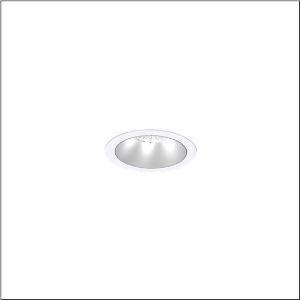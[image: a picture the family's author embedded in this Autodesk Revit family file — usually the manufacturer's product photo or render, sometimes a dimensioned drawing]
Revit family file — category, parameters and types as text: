
# Revit family: lunis_21_m_51db19tc91c
name_source: partatom
category: Lighting Fixtures
units: mm (PartAtom-declared; Revit-internal decimal feet)

## family parameters
Cut with Voids When Loaded = No
Host = Face
Light Source = No
Part Type = Normal
Room Calculation Point = No
Round Connector Dimension = Use Diameter
Shared = No

## types (1)
- --- (1 x LED, 3750 lm, 26 W, 4000K)
    Apparent Load = 26 VA
    CIE Flux Codes = 95 100 100 100 100
    Color Rendering = 80
    Color Temperature = 4000K
    Default Elevation = 1800 mm
    Description = Lunis 21,  M, downlight, light control with lens, of PMMA, anti glare with reflector, of aluminium, matt, light emission: direct distribution, LED rated luminous flux: 1.730lm, light colour: 8tw, with terminal, 5-pole, mains connection: 220..240V, AC/DC, 0/50..60Hz, housing, round, of diecast aluminium, traffic white (RAL 9016), diameter: 115mm, clamping range: 1..40mm, protection rating (complete): IP20, protection rating (on room side): IP54, insulation class (complete): insulation class II (safety insulation), certification: CE, impact resistance: IK03, packaging unit: 1 piece
    Height = 0 mm  [stored 0 ft]
    Lamp = 1 x LED
    Lamp Light Flux = 3750 lm
    Lamp Power = 26 W
    Lamp count = 1
    Length = 115 mm
    Luminous efficacy = 144 lm/W
    Manufacturer = Siteco
    ModVariant = No
    Model = 51DB19TC91C
    Mounting Place = Ceiling
    Mounting Type = Recessed
    Number of Poles = 1
    OnlyDefault = Yes
    Power Factor = 1
    Product Name = Lunis 21 M
    Product group = downlight
    ProductGroupID = 401
    Protection Class = Protection class II
    Protection Degree = IP 20
    RLX_Detail_Level = 1
    RLX_Emergency_Light_Flux = 0 lm
    RLX_Emergency_Type = 0
    RLX_Emergency_Type_DB = No
    RlxData = <blob elided: 11289 chars, md5=7e811bf2>
    Socket = socket
    Standby Power = 0 W
    System Light Flux = 3750 lm
    System Power = 26 W
    Type Comments = individual setting: colour temperature 4000K, luminous flux: 100 % | (ON | ON | OFF | OFF) | 700 mA
    Type Image = l_1290856.jpg
    URL = http://relux.com
    VarID = @adj_025999
    Voltage = 0 V
    Weight = 0.00 kg
    Width = 0 mm  [stored 0 ft]

note: [stored X ft] marks values corroborated as IEEE doubles in the binary element streams (Revit-internal decimal feet)

## geometry (parser evidence)
native form markers: Sweep x9
no freeform markers — native parametric forms only
